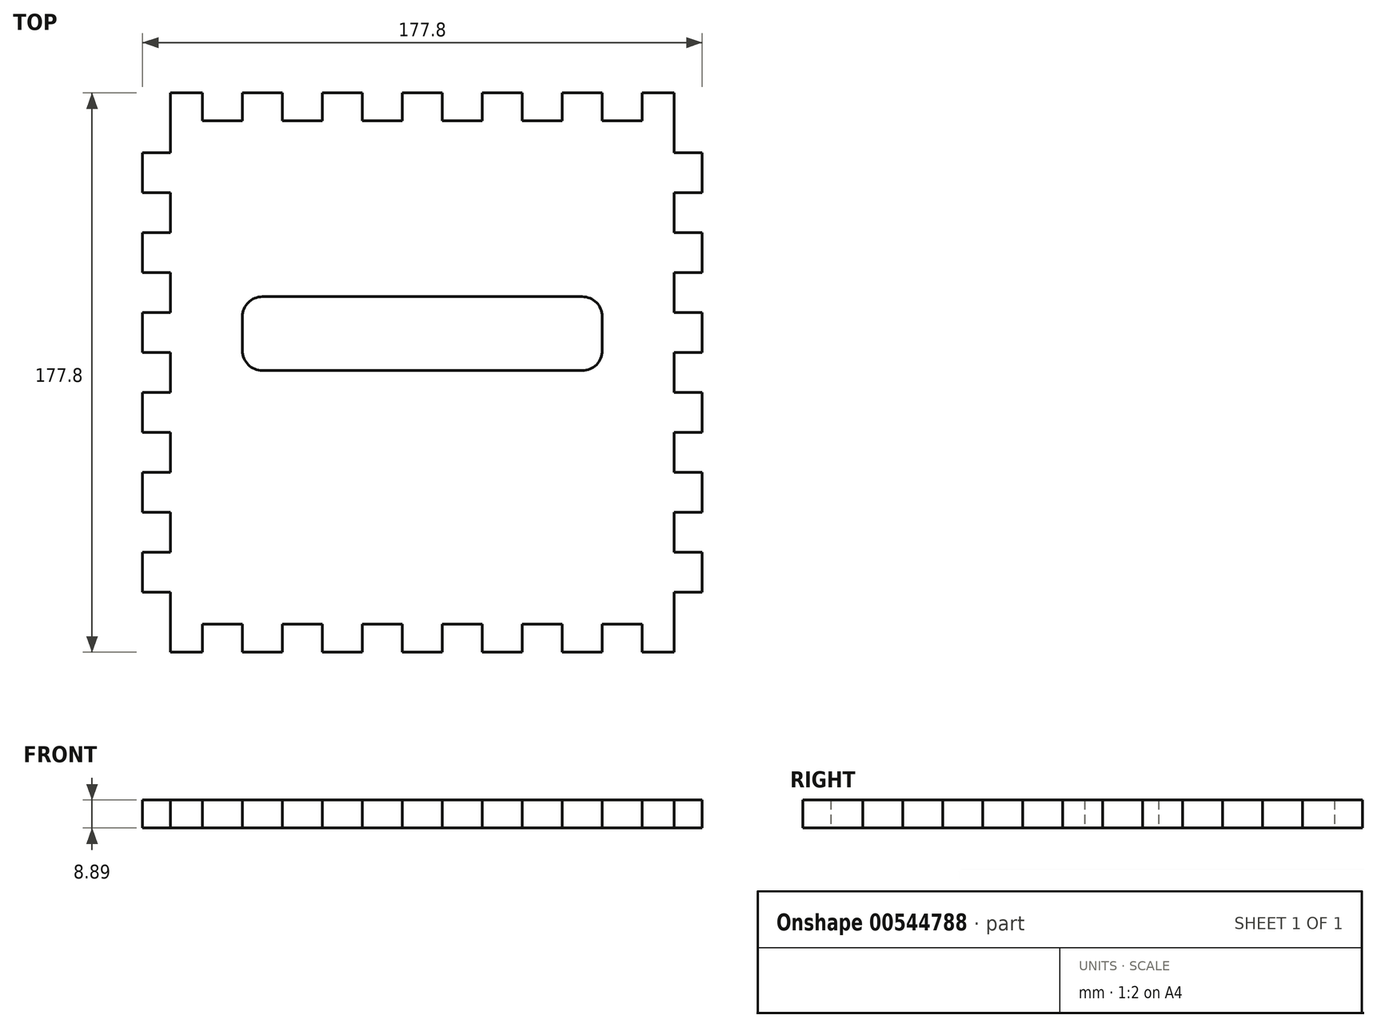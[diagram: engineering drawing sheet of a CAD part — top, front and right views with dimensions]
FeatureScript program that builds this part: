
annotation { "Feature Type Name" : "Feature", "Feature Type Description" : "" }
export const myFeature = defineFeature(function(context is Context, id is Id, definition is map)
    precondition{}
    {
        {
            var Q0;
            Q0=qCreatedBy(makeId("Top.planeOp"),FACE);
            var sketch = newSketch(context, id + "F0", { "sketchPlane" : qUnion([Q0])});
            skLineSegment(sketch, "E0.bottom", {"start": v(8.9, 0) * mm, "end": v(19.05, 0) * mm});
            skLineSegment(sketch, "E0.left", {"start": v(0, -19.05) * mm, "end": v(0, -31.75) * mm});
            skLineSegment(sketch, "E1", {"start": v(8.89, 0) * mm, "end": v(8.9, -19.05) * mm});
            skLineSegment(sketch, "E2", {"start": v(8.9, -19.05) * mm, "end": v(0, -19.05) * mm});
            skLineSegment(sketch, "E3", {"start": v(8.89, 0) * mm, "end": v(19.05, 0) * mm});
            skLineSegment(sketch, "E4", {"start": v(19.05, 0) * mm, "end": v(19.05, -8.9) * mm});
            skLineSegment(sketch, "E5", {"start": v(19.05, -8.9) * mm, "end": v(31.75, -8.9) * mm});
            skLineSegment(sketch, "E6", {"start": v(31.75, -8.9) * mm, "end": v(31.75, 0) * mm});
            skLineSegment(sketch, "E7", {"start": v(31.75, 0) * mm, "end": v(44.45, 0) * mm});
            skLineSegment(sketch, "E8", {"start": v(44.45, 0) * mm, "end": v(44.45, -8.9) * mm});
            skLineSegment(sketch, "E9", {"start": v(44.45, -8.9) * mm, "end": v(57.15, -8.89) * mm});
            skLineSegment(sketch, "E10", {"start": v(57.15, -8.89) * mm, "end": v(57.15, 0) * mm});
            skLineSegment(sketch, "E11", {"start": v(57.15, 0) * mm, "end": v(69.85, 0) * mm});
            skLineSegment(sketch, "E12", {"start": v(69.85, 0) * mm, "end": v(69.85, -8.89) * mm});
            skLineSegment(sketch, "E13", {"start": v(69.85, -8.89) * mm, "end": v(82.55, -8.89) * mm});
            skLineSegment(sketch, "E14", {"start": v(82.55, -8.89) * mm, "end": v(82.55, 0) * mm});
            skLineSegment(sketch, "E15", {"start": v(82.55, 0) * mm, "end": v(95.25, 0) * mm});
            skLineSegment(sketch, "E16", {"start": v(95.25, 0) * mm, "end": v(95.25, -8.89) * mm});
            skLineSegment(sketch, "E17", {"start": v(95.25, -8.89) * mm, "end": v(107.95, -8.89) * mm});
            skLineSegment(sketch, "E18", {"start": v(107.95, -8.89) * mm, "end": v(107.95, 0) * mm});
            skLineSegment(sketch, "E19.trimOffspring", {"start": v(107.95, 0) * mm, "end": v(120.65, 0) * mm});
            skPoint(sketch, "E20.orphan", {"position": v(0, 0) * mm});
            skLineSegment(sketch, "E21", {"start": v(168.9, 0) * mm, "end": v(168.9, -19.05) * mm});
            skLineSegment(sketch, "E22", {"start": v(168.9, -19.05) * mm, "end": v(177.8, -19.05) * mm});
            skPoint(sketch, "E23.orphan", {"position": v(177.8, 0) * mm});
            skLineSegment(sketch, "E24", {"start": v(120.65, 0) * mm, "end": v(120.65, -8.89) * mm});
            skLineSegment(sketch, "E25", {"start": v(120.65, -8.89) * mm, "end": v(133.35, -8.89) * mm});
            skLineSegment(sketch, "E26", {"start": v(133.35, -8.89) * mm, "end": v(133.35, 0) * mm});
            skLineSegment(sketch, "E27", {"start": v(133.35, 0) * mm, "end": v(146.05, 0) * mm});
            skLineSegment(sketch, "E28", {"start": v(146.05, 0) * mm, "end": v(146.05, -8.89) * mm});
            skLineSegment(sketch, "E29", {"start": v(146.05, -8.89) * mm, "end": v(158.75, -8.89) * mm});
            skLineSegment(sketch, "E30", {"start": v(158.75, -8.89) * mm, "end": v(158.75, 0) * mm});
            skLineSegment(sketch, "E31", {"start": v(158.75, 0) * mm, "end": v(168.9, 0) * mm});
            skLineSegment(sketch, "E32", {"start": v(0, -31.75) * mm, "end": v(8.89, -31.75) * mm});
            skLineSegment(sketch, "E33", {"start": v(8.89, -31.75) * mm, "end": v(8.9, -44.45) * mm});
            skLineSegment(sketch, "E34", {"start": v(8.89, -44.45) * mm, "end": v(0, -44.45) * mm});
            skLineSegment(sketch, "E35", {"start": v(0, -44.45) * mm, "end": v(0, -57.15) * mm});
            skLineSegment(sketch, "E36", {"start": v(0, -57.15) * mm, "end": v(8.9, -57.15) * mm});
            skLineSegment(sketch, "E37", {"start": v(8.9, -57.15) * mm, "end": v(8.9, -69.85) * mm});
            skLineSegment(sketch, "E38", {"start": v(8.9, -69.85) * mm, "end": v(0, -69.85) * mm});
            skLineSegment(sketch, "E39", {"start": v(0, -69.85) * mm, "end": v(0, -82.55) * mm});
            skLineSegment(sketch, "E40", {"start": v(0, -82.55) * mm, "end": v(8.9, -82.55) * mm});
            skLineSegment(sketch, "E41", {"start": v(8.9, -82.55) * mm, "end": v(8.9, -95.25) * mm});
            skLineSegment(sketch, "E42", {"start": v(8.9, -95.25) * mm, "end": v(0, -95.25) * mm});
            skLineSegment(sketch, "E43.trimOffspring", {"start": v(0, -95.25) * mm, "end": v(0, -107.95) * mm});
            skLineSegment(sketch, "E44", {"start": v(0, -107.95) * mm, "end": v(8.9, -107.95) * mm});
            skLineSegment(sketch, "E45", {"start": v(8.9, -107.95) * mm, "end": v(8.9, -120.65) * mm});
            skLineSegment(sketch, "E46", {"start": v(8.9, -120.65) * mm, "end": v(0, -120.65) * mm});
            skLineSegment(sketch, "E47", {"start": v(0, -120.65) * mm, "end": v(0, -133.35) * mm});
            skLineSegment(sketch, "E48", {"start": v(0, -133.35) * mm, "end": v(8.9, -133.35) * mm});
            skLineSegment(sketch, "E49", {"start": v(8.9, -133.35) * mm, "end": v(8.9, -146.05) * mm});
            skLineSegment(sketch, "E50", {"start": v(8.9, -146.05) * mm, "end": v(0, -146.05) * mm});
            skLineSegment(sketch, "E51", {"start": v(0, -146.05) * mm, "end": v(0, -158.75) * mm});
            skLineSegment(sketch, "E52", {"start": v(0, -158.75) * mm, "end": v(8.9, -158.75) * mm});
            skLineSegment(sketch, "E53", {"start": v(8.9, -158.75) * mm, "end": v(8.9, -177.8) * mm});
            skPoint(sketch, "E54.orphan", {"position": v(0, -177.8) * mm});
            skLineSegment(sketch, "E55", {"start": v(88.9, 0) * mm, "end": v(88.9, -44.12) * mm, "construction": true});
            skLineSegment(sketch, "E56", {"start": v(8.9, -88.9) * mm, "end": v(47.76, -88.9) * mm, "construction": true});
            skPoint(sketch, "E56.endSnap0", {"position": v(8.9, -88.9) * mm});
            skLineSegment(sketch, "E57.MirrorCS", {"start": v(8.89, -177.8) * mm, "end": v(19.05, -177.8) * mm});
            skLineSegment(sketch, "E58.MirrorCS", {"start": v(19.05, -177.8) * mm, "end": v(19.05, -168.91) * mm});
            skLineSegment(sketch, "E59.MirrorCS", {"start": v(31.75, -168.91) * mm, "end": v(31.75, -177.8) * mm});
            skLineSegment(sketch, "E60.MirrorCS", {"start": v(31.75, -177.8) * mm, "end": v(44.45, -177.8) * mm});
            skLineSegment(sketch, "E61.MirrorCS", {"start": v(44.45, -177.8) * mm, "end": v(44.45, -168.91) * mm});
            skLineSegment(sketch, "E62.MirrorCS", {"start": v(44.45, -168.91) * mm, "end": v(57.15, -168.91) * mm});
            skLineSegment(sketch, "E63.MirrorCS", {"start": v(57.15, -168.91) * mm, "end": v(57.15, -177.8) * mm});
            skLineSegment(sketch, "E64.MirrorCS", {"start": v(57.15, -177.8) * mm, "end": v(69.85, -177.8) * mm});
            skLineSegment(sketch, "E65.MirrorCS", {"start": v(69.85, -177.8) * mm, "end": v(69.85, -168.91) * mm});
            skLineSegment(sketch, "E66.MirrorCS", {"start": v(69.85, -168.91) * mm, "end": v(82.55, -168.91) * mm});
            skLineSegment(sketch, "E67.MirrorCS", {"start": v(82.55, -168.91) * mm, "end": v(82.55, -177.8) * mm});
            skLineSegment(sketch, "E68.MirrorCS", {"start": v(82.55, -177.8) * mm, "end": v(95.25, -177.8) * mm});
            skLineSegment(sketch, "E69.MirrorCS", {"start": v(95.25, -177.8) * mm, "end": v(95.25, -168.91) * mm});
            skLineSegment(sketch, "E70.MirrorCS", {"start": v(95.25, -168.91) * mm, "end": v(107.95, -168.91) * mm});
            skLineSegment(sketch, "E71.MirrorCS", {"start": v(107.95, -168.91) * mm, "end": v(107.95, -177.8) * mm});
            skLineSegment(sketch, "E72.MirrorCS", {"start": v(107.95, -177.8) * mm, "end": v(120.65, -177.8) * mm});
            skLineSegment(sketch, "E73.MirrorCS", {"start": v(120.65, -177.8) * mm, "end": v(120.65, -168.91) * mm});
            skLineSegment(sketch, "E74.MirrorCS", {"start": v(120.65, -168.91) * mm, "end": v(133.35, -168.91) * mm});
            skLineSegment(sketch, "E75.MirrorCS", {"start": v(133.35, -168.91) * mm, "end": v(133.35, -177.8) * mm});
            skLineSegment(sketch, "E76.MirrorCS", {"start": v(133.35, -177.8) * mm, "end": v(146.05, -177.8) * mm});
            skLineSegment(sketch, "E77.MirrorCS", {"start": v(146.05, -177.8) * mm, "end": v(146.05, -168.91) * mm});
            skLineSegment(sketch, "E78.MirrorCS", {"start": v(146.05, -168.91) * mm, "end": v(158.75, -168.91) * mm});
            skLineSegment(sketch, "E79.MirrorCS", {"start": v(158.75, -168.91) * mm, "end": v(158.75, -177.8) * mm});
            skLineSegment(sketch, "E80.MirrorCS", {"start": v(158.75, -177.8) * mm, "end": v(168.9, -177.8) * mm});
            skLineSegment(sketch, "E81.MirrorCS", {"start": v(168.9, -177.8) * mm, "end": v(168.9, -158.75) * mm});
            skLineSegment(sketch, "E82.MirrorCS", {"start": v(168.9, -158.75) * mm, "end": v(177.8, -158.75) * mm});
            skLineSegment(sketch, "E83.MirrorCS", {"start": v(177.8, -19.05) * mm, "end": v(177.8, -31.75) * mm});
            skLineSegment(sketch, "E84.MirrorCS", {"start": v(177.8, -31.75) * mm, "end": v(168.91, -31.75) * mm});
            skLineSegment(sketch, "E85.MirrorCS", {"start": v(168.91, -31.75) * mm, "end": v(168.91, -44.45) * mm});
            skLineSegment(sketch, "E86.MirrorCS", {"start": v(168.91, -44.45) * mm, "end": v(177.8, -44.45) * mm});
            skLineSegment(sketch, "E87.MirrorCS", {"start": v(177.8, -44.45) * mm, "end": v(177.8, -57.15) * mm});
            skLineSegment(sketch, "E88.MirrorCS", {"start": v(177.8, -57.15) * mm, "end": v(168.91, -57.15) * mm});
            skLineSegment(sketch, "E89.MirrorCS", {"start": v(168.91, -57.15) * mm, "end": v(168.91, -69.85) * mm});
            skLineSegment(sketch, "E90.MirrorCS", {"start": v(168.91, -69.85) * mm, "end": v(177.8, -69.85) * mm});
            skLineSegment(sketch, "E91.MirrorCS", {"start": v(177.8, -69.85) * mm, "end": v(177.8, -82.55) * mm});
            skLineSegment(sketch, "E92.MirrorCS", {"start": v(177.8, -82.55) * mm, "end": v(168.91, -82.55) * mm});
            skLineSegment(sketch, "E93.MirrorCS", {"start": v(168.91, -82.55) * mm, "end": v(168.91, -95.25) * mm});
            skLineSegment(sketch, "E94.MirrorCS", {"start": v(168.91, -95.25) * mm, "end": v(177.8, -95.25) * mm});
            skLineSegment(sketch, "E95.MirrorCS", {"start": v(177.8, -95.25) * mm, "end": v(177.8, -107.95) * mm});
            skLineSegment(sketch, "E96.MirrorCS", {"start": v(177.8, -107.95) * mm, "end": v(168.91, -107.95) * mm});
            skLineSegment(sketch, "E97.MirrorCS", {"start": v(168.91, -107.95) * mm, "end": v(168.91, -120.65) * mm});
            skLineSegment(sketch, "E98.MirrorCS", {"start": v(168.91, -120.65) * mm, "end": v(177.8, -120.65) * mm});
            skLineSegment(sketch, "E99.MirrorCS", {"start": v(177.8, -120.65) * mm, "end": v(177.8, -133.35) * mm});
            skLineSegment(sketch, "E100.MirrorCS", {"start": v(177.8, -133.35) * mm, "end": v(168.91, -133.35) * mm});
            skLineSegment(sketch, "E101.MirrorCS", {"start": v(168.91, -133.35) * mm, "end": v(168.91, -146.05) * mm});
            skLineSegment(sketch, "E102.MirrorCS", {"start": v(168.91, -146.05) * mm, "end": v(177.8, -146.05) * mm});
            skLineSegment(sketch, "E103.MirrorCS", {"start": v(177.8, -146.05) * mm, "end": v(177.8, -158.75) * mm});
            skLineSegment(sketch, "E104.MirrorCS", {"start": v(177.8, -158.75) * mm, "end": v(168.91, -158.75) * mm});
            skLineSegment(sketch, "E105", {"start": v(19.05, -168.91) * mm, "end": v(31.75, -168.91) * mm});
            skLineSegment(sketch, "E106.bottom", {"start": v(38.1, -64.77) * mm, "end": v(139.7, -64.77) * mm});
            skLineSegment(sketch, "E106.top", {"start": v(38.1, -88.27) * mm, "end": v(139.7, -88.27) * mm});
            skLineSegment(sketch, "E106.left", {"start": v(31.75, -71.12) * mm, "end": v(31.75, -81.92) * mm});
            skLineSegment(sketch, "E106.right", {"start": v(146.05, -71.12) * mm, "end": v(146.05, -81.92) * mm});
            skLineSegment(sketch, "E107", {"start": v(88.9, 0) * mm, "end": v(88.9, -64.77) * mm, "construction": true});
            skPoint(sketch, "E108.visualSharp", {"position": v(31.75, -64.77) * mm});
            skArc(sketch, "E108.filletArc", {"start": v(38.1, -64.77) * mm, "mid": v(33.6, -66.63) * mm, "end": v(31.75, -71.12) * mm});
            skPoint(sketch, "E109.visualSharp", {"position": v(31.75, -88.27) * mm});
            skArc(sketch, "E109.filletArc", {"start": v(31.75, -81.92) * mm, "mid": v(33.6, -86.4) * mm, "end": v(38.1, -88.27) * mm});
            skPoint(sketch, "E110.visualSharp", {"position": v(146.05, -88.27) * mm});
            skArc(sketch, "E110.filletArc", {"start": v(139.7, -88.27) * mm, "mid": v(144.2, -86.4) * mm, "end": v(146.05, -81.92) * mm});
            skPoint(sketch, "E111.visualSharp", {"position": v(146.05, -64.77) * mm});
            skArc(sketch, "E111.filletArc", {"start": v(146.05, -71.12) * mm, "mid": v(144.2, -66.63) * mm, "end": v(139.7, -64.77) * mm});
            skSolve(sketch);
        }
        {
            var Q0;
            Q0=makeQuery(id+"F0.imprint","IMPRINT",FACE,{"disambiguationData":[TD([[makeQuery(id+"F0.imprint","IMPRINT",EDGE,{"derivedFrom":sQuery(id+"F0.wireOp",EDGE,"E1")}),1.0]])]});
            extrude(context, id + "F1", {"entities" : qUnion([Q0]), "depth" : 8.9 * mm, "offsetDistance" : 25.4 * mm});
        }
    });
